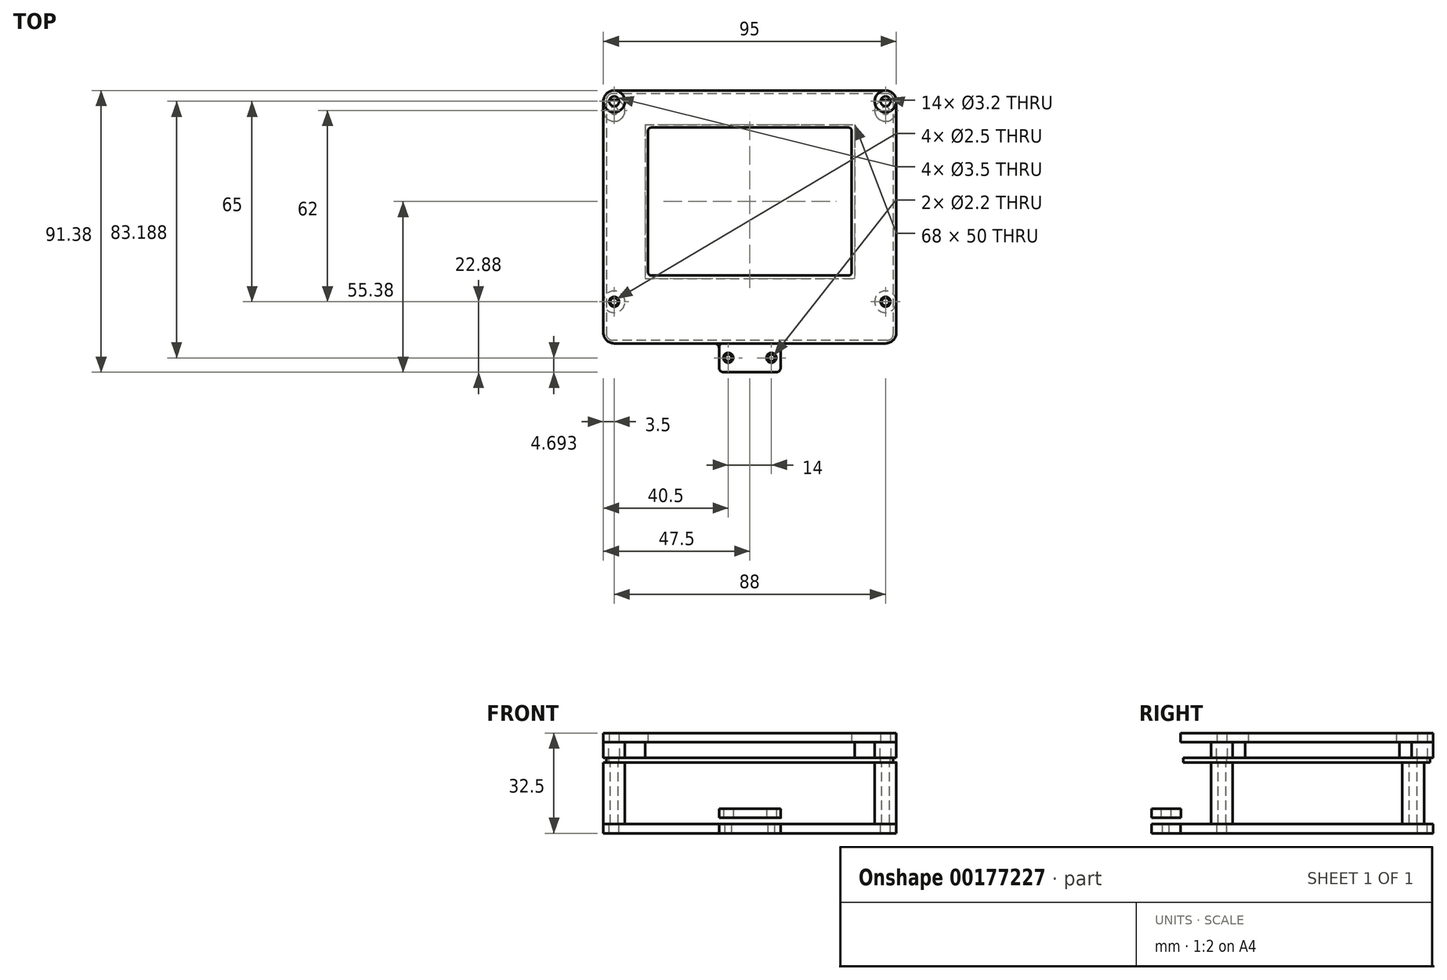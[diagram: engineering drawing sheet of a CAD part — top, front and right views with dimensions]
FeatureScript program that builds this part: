
annotation { "Feature Type Name" : "Feature", "Feature Type Description" : "" }
export const myFeature = defineFeature(function(context is Context, id is Id, definition is map)
    precondition{}
    {
        {
            var Q0;
            Q0=qCreatedBy(makeId("Top.planeOp"),FACE);
            var sketch = newSketch(context, id + "F0", { "sketchPlane" : qUnion([Q0])});
            skLineSegment(sketch, "E0.bottom", {"start": v(44, -41) * mm, "end": v(-44, -41) * mm});
            skLineSegment(sketch, "E0.top", {"start": v(44, 41) * mm, "end": v(-44, 41) * mm});
            skLineSegment(sketch, "E0.left", {"start": v(47.5, -37.5) * mm, "end": v(47.5, 37.5) * mm});
            skLineSegment(sketch, "E0.right", {"start": v(-47.5, -37.5) * mm, "end": v(-47.5, 37.5) * mm});
            skPoint(sketch, "E0.middle", {"position": v(0, 0) * mm});
            skLineSegment(sketch, "E1.top", {"start": v(44, 37.5) * mm, "end": v(-44, 37.5) * mm, "construction": true});
            skLineSegment(sketch, "E1.left", {"start": v(44, -27.5) * mm, "end": v(44, 37.5) * mm, "construction": true});
            skLineSegment(sketch, "E1.right", {"start": v(-44, -27.5) * mm, "end": v(-44, 37.5) * mm, "construction": true});
            skLineSegment(sketch, "E2", {"start": v(-44, -27.5) * mm, "end": v(44, -27.5) * mm, "construction": true});
            skPoint(sketch, "E1.bottom.end.orphan", {"position": v(-44, -37.5) * mm});
            skPoint(sketch, "E3.orphan", {"position": v(44, -37.5) * mm});
            skCircle(sketch, "E4", {"center": v(-44, 37.5) * mm, "radius": 1.6 * mm});
            skCircle(sketch, "E5", {"center": v(44, 37.5) * mm, "radius": 1.6 * mm});
            skCircle(sketch, "E6", {"center": v(44, -27.5) * mm, "radius": 1.6 * mm});
            skCircle(sketch, "E7", {"center": v(-44, -27.5) * mm, "radius": 1.6 * mm});
            skArc(sketch, "E8", {"start": v(-44, 41) * mm, "mid": v(-46.47, 39.97) * mm, "end": v(-47.5, 37.5) * mm});
            skArc(sketch, "E9", {"start": v(47.5, 37.5) * mm, "mid": v(46.47, 39.97) * mm, "end": v(44, 41) * mm});
            skPoint(sketch, "E10.visualSharp", {"position": v(47.5, -41) * mm});
            skArc(sketch, "E10.filletArc", {"start": v(44, -41) * mm, "mid": v(46.47, -39.97) * mm, "end": v(47.5, -37.5) * mm});
            skPoint(sketch, "E11.visualSharp", {"position": v(-47.5, -41) * mm});
            skArc(sketch, "E11.filletArc", {"start": v(-47.5, -37.5) * mm, "mid": v(-46.47, -39.97) * mm, "end": v(-44, -41) * mm});
            skPoint(sketch, "E12.orphan", {"position": v(-47.5, 41) * mm});
            skPoint(sketch, "E13.orphan", {"position": v(47.5, 41) * mm});
            skLineSegment(sketch, "E14.bottom", {"start": v(-32, 29) * mm, "end": v(32, 29) * mm});
            skLineSegment(sketch, "E14.top", {"start": v(-32, -19) * mm, "end": v(32, -19) * mm});
            skLineSegment(sketch, "E14.left", {"start": v(-33, 28) * mm, "end": v(-33, -18) * mm});
            skLineSegment(sketch, "E14.right", {"start": v(33, 28) * mm, "end": v(33, -18) * mm});
            skPoint(sketch, "E15.visualSharp", {"position": v(-33, 29) * mm});
            skArc(sketch, "E15.filletArc", {"start": v(-32, 29) * mm, "mid": v(-32.7, 28.7) * mm, "end": v(-33, 28) * mm});
            skPoint(sketch, "E16.visualSharp", {"position": v(33, 29) * mm});
            skArc(sketch, "E16.filletArc", {"start": v(33, 28) * mm, "mid": v(32.7, 28.7) * mm, "end": v(32, 29) * mm});
            skPoint(sketch, "E17.visualSharp", {"position": v(33, -19) * mm});
            skArc(sketch, "E17.filletArc", {"start": v(32, -19) * mm, "mid": v(32.7, -18.7) * mm, "end": v(33, -18) * mm});
            skPoint(sketch, "E18.visualSharp", {"position": v(-33, -19) * mm});
            skArc(sketch, "E18.filletArc", {"start": v(-33, -18) * mm, "mid": v(-32.7, -18.7) * mm, "end": v(-32, -19) * mm});
            skSolve(sketch);
        }
        {
            var Q0;
            Q0=makeQuery(id+"F0.imprint","IMPRINT",FACE,{"disambiguationData":[TD([[makeQuery(id+"F0.imprint","IMPRINT",EDGE,{"derivedFrom":sQuery(id+"F0.wireOp",EDGE,"E0.bottom")}),-1.0]])]});
            extrude(context, id + "F1", {"entities" : qUnion([Q0]), "depth" : 3 * mm});
        }
        {
            var Q0;
            Q0=makeQuery(id+"F1.opExtrude","CAP_FACE",FACE,{"disambiguationData":[OSD([sQuery(id+"F0.wireOp",EDGE,"E0.bottom"),sQuery(id+"F0.wireOp",EDGE,"E0.top"),sQuery(id+"F0.wireOp",EDGE,"E0.left"),sQuery(id+"F0.wireOp",EDGE,"E0.right"),sQuery(id+"F0.wireOp",EDGE,"E4"),sQuery(id+"F0.wireOp",EDGE,"E5"),sQuery(id+"F0.wireOp",EDGE,"E6"),sQuery(id+"F0.wireOp",EDGE,"E7"),sQuery(id+"F0.wireOp",EDGE,"E8"),sQuery(id+"F0.wireOp",EDGE,"E9"),sQuery(id+"F0.wireOp",EDGE,"E10.filletArc"),sQuery(id+"F0.wireOp",EDGE,"E11.filletArc"),sQuery(id+"F0.wireOp",EDGE,"E14.bottom"),sQuery(id+"F0.wireOp",EDGE,"E14.top"),sQuery(id+"F0.wireOp",EDGE,"E14.left"),sQuery(id+"F0.wireOp",EDGE,"E14.right"),sQuery(id+"F0.wireOp",EDGE,"E15.filletArc"),sQuery(id+"F0.wireOp",EDGE,"E16.filletArc"),sQuery(id+"F0.wireOp",EDGE,"E17.filletArc"),sQuery(id+"F0.wireOp",EDGE,"E18.filletArc")])],"isStart":true});
            var sketch = newSketch(context, id + "F2", { "sketchPlane" : qUnion([Q0])});
            skCircle(sketch, "E19", {"center": v(-44, 27.5) * mm, "radius": 1.75 * mm});
            skCircle(sketch, "E20", {"center": v(44, 27.5) * mm, "radius": 1.75 * mm});
            skCircle(sketch, "E21", {"center": v(44, -37.5) * mm, "radius": 1.75 * mm});
            skCircle(sketch, "E22", {"center": v(-44, -37.5) * mm, "radius": 1.75 * mm});
            skCircle(sketch, "E23", {"center": v(-44, -37.5) * mm, "radius": 3.5 * mm});
            skCircle(sketch, "E24", {"center": v(44, -37.5) * mm, "radius": 3.5 * mm});
            skCircle(sketch, "E25", {"center": v(44, 27.5) * mm, "radius": 3.5 * mm});
            skCircle(sketch, "E26", {"center": v(-44, 27.5) * mm, "radius": 3.5 * mm});
            skSolve(sketch);
        }
        {
            var Q0;
            Q0 = qSketchRegion(id + "F2", true);
            extrude(context, id + "F3", {"entities" : qUnion([Q0]), "depth" : 5 * mm});
        }
        {
            var Q0;
            Q0=makeQuery(id+"F3.opExtrude","CAP_FACE",FACE,{"disambiguationData":[OSD([sQuery(id+"F2.wireOp",EDGE,"E19"),sQuery(id+"F2.wireOp",EDGE,"E26")])],"isStart":false});
            var sketch = newSketch(context, id + "F4", { "sketchPlane" : qUnion([Q0])});
            skLineSegment(sketch, "E27.bottom", {"start": v(44.5, -40) * mm, "end": v(-44.5, -40) * mm});
            skLineSegment(sketch, "E27.top", {"start": v(44.5, 40) * mm, "end": v(-44.5, 40) * mm});
            skLineSegment(sketch, "E27.left", {"start": v(46.5, -38) * mm, "end": v(46.5, 38) * mm});
            skLineSegment(sketch, "E27.right", {"start": v(-46.5, -38) * mm, "end": v(-46.5, 38) * mm});
            skPoint(sketch, "E27.middle", {"position": v(0, 0) * mm});
            skPoint(sketch, "E28.visualSharp", {"position": v(-46.5, 40) * mm});
            skArc(sketch, "E28.filletArc", {"start": v(-44.5, 40) * mm, "mid": v(-45.91, 39.41) * mm, "end": v(-46.5, 38) * mm});
            skPoint(sketch, "E29.visualSharp", {"position": v(46.5, 40) * mm});
            skArc(sketch, "E29.filletArc", {"start": v(46.5, 38) * mm, "mid": v(45.91, 39.41) * mm, "end": v(44.5, 40) * mm});
            skPoint(sketch, "E30.visualSharp", {"position": v(46.5, -40) * mm});
            skArc(sketch, "E30.filletArc", {"start": v(44.5, -40) * mm, "mid": v(45.91, -39.41) * mm, "end": v(46.5, -38) * mm});
            skPoint(sketch, "E31.visualSharp", {"position": v(-46.5, -40) * mm});
            skArc(sketch, "E31.filletArc", {"start": v(-46.5, -38) * mm, "mid": v(-45.91, -39.41) * mm, "end": v(-44.5, -40) * mm});
            skCircle(sketch, "E32", {"center": v(-44, 27.5) * mm, "radius": 1.6 * mm});
            skCircle(sketch, "E33.0.1.0", {"center": v(-44, -37.5) * mm, "radius": 1.6 * mm});
            skCircle(sketch, "E33.1.0.0", {"center": v(44, 27.5) * mm, "radius": 1.6 * mm});
            skCircle(sketch, "E33.1.1.0", {"center": v(44, -37.5) * mm, "radius": 1.6 * mm});
            skCircle(sketch, "E33.2.0.0", {"center": v(132, 27.5) * mm, "radius": 1.6 * mm});
            skCircle(sketch, "E33.2.1.0", {"center": v(132, -37.5) * mm, "radius": 1.6 * mm});
            skLineSegment(sketch, "E33.direction1", {"start": v(-44, 27.5) * mm, "end": v(44, 27.5) * mm, "construction": true});
            skLineSegment(sketch, "E33.direction2", {"start": v(-44, 27.5) * mm, "end": v(-44, -37.5) * mm, "construction": true});
            skSolve(sketch);
        }
        {
            var Q0;
            Q0 = qSketchRegion(id + "F4", true);
            extrude(context, id + "F5", {"entities" : qUnion([Q0]), "depth" : 1.5 * mm});
        }
        {
            var Q0;
            Q0=makeQuery(id+"F5.opExtrude","CAP_FACE",FACE,{"disambiguationData":[OSD([sQuery(id+"F4.wireOp",EDGE,"E27.bottom"),sQuery(id+"F4.wireOp",EDGE,"E27.top"),sQuery(id+"F4.wireOp",EDGE,"E27.left"),sQuery(id+"F4.wireOp",EDGE,"E27.right"),sQuery(id+"F4.wireOp",EDGE,"E28.filletArc"),sQuery(id+"F4.wireOp",EDGE,"E29.filletArc"),sQuery(id+"F4.wireOp",EDGE,"E30.filletArc"),sQuery(id+"F4.wireOp",EDGE,"E31.filletArc"),sQuery(id+"F4.wireOp",EDGE,"E32"),sQuery(id+"F4.wireOp",EDGE,"E33.0.1.0"),sQuery(id+"F4.wireOp",EDGE,"E33.1.0.0"),sQuery(id+"F4.wireOp",EDGE,"E33.1.1.0")])],"isStart":false});
            var sketch = newSketch(context, id + "F6", { "sketchPlane" : qUnion([Q0])});
            skCircle(sketch, "E34", {"center": v(-44, 27.5) * mm, "radius": 1.25 * mm});
            skCircle(sketch, "E35", {"center": v(-44, 27.5) * mm, "radius": 3.5 * mm});
            skCircle(sketch, "E36.0.1.0", {"center": v(-44, -34.5) * mm, "radius": 1.25 * mm});
            skCircle(sketch, "E36.0.1.1", {"center": v(-44, -34.5) * mm, "radius": 3.5 * mm});
            skCircle(sketch, "E36.1.0.0", {"center": v(44, 27.5) * mm, "radius": 1.25 * mm});
            skCircle(sketch, "E36.1.0.1", {"center": v(44, 27.5) * mm, "radius": 3.5 * mm});
            skCircle(sketch, "E36.1.1.0", {"center": v(44, -34.5) * mm, "radius": 1.25 * mm});
            skCircle(sketch, "E36.1.1.1", {"center": v(44, -34.5) * mm, "radius": 3.5 * mm});
            skLineSegment(sketch, "E36.direction1", {"start": v(-44, 27.5) * mm, "end": v(44, 27.5) * mm, "construction": true});
            skLineSegment(sketch, "E36.direction2", {"start": v(-44, 27.5) * mm, "end": v(-44, -34.5) * mm, "construction": true});
            skSolve(sketch);
        }
        {
            var Q0;
            Q0 = qSketchRegion(id + "F6", true);
            extrude(context, id + "F7", {"entities" : qUnion([Q0]), "depth" : 20 * mm});
        }
        {
            var Q0;
            Q0=makeQuery(id+"F7.opExtrude","CAP_FACE",FACE,{"disambiguationData":[OSD([sQuery(id+"F6.wireOp",EDGE,"E34"),sQuery(id+"F6.wireOp",EDGE,"E35")])],"isStart":false});
            var sketch = newSketch(context, id + "F8", { "sketchPlane" : qUnion([Q0])});
            skLineSegment(sketch, "E37.bottom", {"start": v(44, -41) * mm, "end": v(-44, -41) * mm});
            skLineSegment(sketch, "E37.top", {"start": v(44, 41) * mm, "end": v(11.5, 41) * mm});
            skLineSegment(sketch, "E37.left", {"start": v(47.5, -37.5) * mm, "end": v(47.5, 37.5) * mm});
            skLineSegment(sketch, "E37.right", {"start": v(-47.5, -37.5) * mm, "end": v(-47.5, 37.5) * mm});
            skPoint(sketch, "E37.middle", {"position": v(0, 0) * mm});
            skPoint(sketch, "E38.visualSharp", {"position": v(47.5, 41) * mm});
            skArc(sketch, "E38.filletArc", {"start": v(47.5, 37.5) * mm, "mid": v(46.47, 39.97) * mm, "end": v(44, 41) * mm});
            skPoint(sketch, "E39.visualSharp", {"position": v(47.5, -41) * mm});
            skArc(sketch, "E39.filletArc", {"start": v(44, -41) * mm, "mid": v(46.47, -39.97) * mm, "end": v(47.5, -37.5) * mm});
            skPoint(sketch, "E40.visualSharp", {"position": v(-47.5, -41) * mm});
            skArc(sketch, "E40.filletArc", {"start": v(-47.5, -37.5) * mm, "mid": v(-46.47, -39.97) * mm, "end": v(-44, -41) * mm});
            skPoint(sketch, "E41.visualSharp", {"position": v(-47.5, 41) * mm});
            skArc(sketch, "E41.filletArc", {"start": v(-44, 41) * mm, "mid": v(-46.47, 39.97) * mm, "end": v(-47.5, 37.5) * mm});
            skCircle(sketch, "E42", {"center": v(-44, 27.5) * mm, "radius": 1.6 * mm});
            skCircle(sketch, "E43.0.1.0", {"center": v(-44, -37.5) * mm, "radius": 1.6 * mm});
            skCircle(sketch, "E43.1.0.0", {"center": v(44, 27.5) * mm, "radius": 1.6 * mm});
            skCircle(sketch, "E43.1.1.0", {"center": v(44, -37.5) * mm, "radius": 1.6 * mm});
            skLineSegment(sketch, "E43.direction1", {"start": v(-44, 27.5) * mm, "end": v(44, 27.5) * mm, "construction": true});
            skLineSegment(sketch, "E43.direction2", {"start": v(-44, 27.5) * mm, "end": v(-44, -37.5) * mm, "construction": true});
            skLineSegment(sketch, "E44.top", {"start": v(8.5, 50.37) * mm, "end": v(-8.5, 50.37) * mm});
            skLineSegment(sketch, "E44.left", {"start": v(10, 42.5) * mm, "end": v(10, 48.87) * mm});
            skLineSegment(sketch, "E44.right", {"start": v(-10, 42.5) * mm, "end": v(-10, 48.87) * mm});
            skPoint(sketch, "E44.middle", {"position": v(0, 41) * mm});
            skPoint(sketch, "E44.bottom.end.orphan", {"position": v(-10, 31.62) * mm});
            skPoint(sketch, "E45.orphan", {"position": v(10, 31.62) * mm});
            skLineSegment(sketch, "E46.trimOffspring", {"start": v(-11.5, 41) * mm, "end": v(-44, 41) * mm});
            skPoint(sketch, "E47.visualSharp", {"position": v(-10, 41) * mm});
            skArc(sketch, "E47.filletArc", {"start": v(-11.5, 41) * mm, "mid": v(-10.44, 41.44) * mm, "end": v(-10, 42.5) * mm});
            skPoint(sketch, "E48.visualSharp", {"position": v(10, 41) * mm});
            skArc(sketch, "E48.filletArc", {"start": v(10, 42.5) * mm, "mid": v(10.44, 41.44) * mm, "end": v(11.5, 41) * mm});
            skPoint(sketch, "E49.visualSharp", {"position": v(10, 50.37) * mm});
            skArc(sketch, "E49.filletArc", {"start": v(10, 48.87) * mm, "mid": v(9.56, 49.94) * mm, "end": v(8.5, 50.37) * mm});
            skPoint(sketch, "E50.visualSharp", {"position": v(-10, 50.37) * mm});
            skArc(sketch, "E50.filletArc", {"start": v(-8.5, 50.37) * mm, "mid": v(-9.56, 49.94) * mm, "end": v(-10, 48.87) * mm});
            skLineSegment(sketch, "E51", {"start": v(-10, 45.69) * mm, "end": v(10, 45.69) * mm, "construction": true});
            skCircle(sketch, "E52", {"center": v(-7, 45.69) * mm, "radius": 1.1 * mm});
            skCircle(sketch, "E53", {"center": v(7, 45.69) * mm, "radius": 1.1 * mm});
            skSolve(sketch);
        }
        {
            var Q0;
            Q0 = qSketchRegion(id + "F8", true);
            extrude(context, id + "F9", {"entities" : qUnion([Q0]), "depth" : 3 * mm});
        }
        {
            var Q0;
            Q0=makeQuery(id+"F9.opExtrude","CAP_FACE",FACE,{"disambiguationData":[OSD([sQuery(id+"F8.wireOp",EDGE,"E37.bottom"),sQuery(id+"F8.wireOp",EDGE,"E37.top"),sQuery(id+"F8.wireOp",EDGE,"E37.left"),sQuery(id+"F8.wireOp",EDGE,"E37.right"),sQuery(id+"F8.wireOp",EDGE,"E38.filletArc"),sQuery(id+"F8.wireOp",EDGE,"E39.filletArc"),sQuery(id+"F8.wireOp",EDGE,"E40.filletArc"),sQuery(id+"F8.wireOp",EDGE,"E41.filletArc"),sQuery(id+"F8.wireOp",EDGE,"E42"),sQuery(id+"F8.wireOp",EDGE,"E43.0.1.0"),sQuery(id+"F8.wireOp",EDGE,"E43.1.0.0"),sQuery(id+"F8.wireOp",EDGE,"E43.1.1.0"),sQuery(id+"F8.wireOp",EDGE,"E44.top"),sQuery(id+"F8.wireOp",EDGE,"E44.left"),sQuery(id+"F8.wireOp",EDGE,"E44.right"),sQuery(id+"F8.wireOp",EDGE,"E46.trimOffspring"),sQuery(id+"F8.wireOp",EDGE,"E47.filletArc"),sQuery(id+"F8.wireOp",EDGE,"E48.filletArc"),sQuery(id+"F8.wireOp",EDGE,"E49.filletArc"),sQuery(id+"F8.wireOp",EDGE,"E50.filletArc"),sQuery(id+"F8.wireOp",EDGE,"E52"),sQuery(id+"F8.wireOp",EDGE,"E53")])],"isStart":true});
            cPlane(context, id + "F10", {"entities" : qUnion([Q0]), "cplaneType" : CPlaneType.OFFSET, "offset" : 2 * mm, "width" : 150 * mm, "height" : 150 * mm});
        }
        {
            var Q0;
            Q0=qCreatedBy(id+"F10.planeOp",FACE);
            var sketch = newSketch(context, id + "F11", { "sketchPlane" : qUnion([Q0])});
            skLineSegment(sketch, "E54.0", {"start": v(10, -42.37) * mm, "end": v(10, -48.87) * mm});
            skLineSegment(sketch, "E55.0", {"start": v(8.5, -50.37) * mm, "end": v(-8.5, -50.37) * mm});
            skLineSegment(sketch, "E56.0", {"start": v(-10, -42.37) * mm, "end": v(-10, -48.87) * mm});
            skLineSegment(sketch, "E57", {"start": v(-8.5, -40.87) * mm, "end": v(8.5, -40.87) * mm});
            skPoint(sketch, "E58.newPointA", {"position": v(10, -48.87) * mm});
            skPoint(sketch, "E58.newPointB", {"position": v(8.5, -50.37) * mm});
            skArc(sketch, "E58.filletArc", {"start": v(8.5, -50.37) * mm, "mid": v(9.56, -49.94) * mm, "end": v(10, -48.87) * mm});
            skPoint(sketch, "E59.newPointA", {"position": v(-8.5, -50.37) * mm});
            skPoint(sketch, "E59.newPointB", {"position": v(-10, -48.87) * mm});
            skArc(sketch, "E59.filletArc", {"start": v(-10, -48.87) * mm, "mid": v(-9.56, -49.94) * mm, "end": v(-8.5, -50.37) * mm});
            skPoint(sketch, "E60.newPointA", {"position": v(-10, -42.5) * mm});
            skArc(sketch, "E60.filletArc", {"start": v(-8.5, -40.87) * mm, "mid": v(-9.56, -41.31) * mm, "end": v(-10, -42.37) * mm});
            skPoint(sketch, "E61.newPointB", {"position": v(10, -42.5) * mm});
            skArc(sketch, "E61.filletArc", {"start": v(10, -42.37) * mm, "mid": v(9.56, -41.31) * mm, "end": v(8.5, -40.88) * mm});
            skCircle(sketch, "E62", {"center": v(-7, -45.69) * mm, "radius": 1.6 * mm});
            skCircle(sketch, "E63", {"center": v(7, -45.69) * mm, "radius": 1.6 * mm});
            skSolve(sketch);
        }
        {
            var Q0;
            Q0 = qSketchRegion(id + "F11", true);
            extrude(context, id + "F12", {"entities" : qUnion([Q0]), "depth" : 3 * mm});
        }
        {
            var Q0;
            Q0=makeQuery(id+"F5.opExtrude","CAP_FACE",FACE,{"disambiguationData":[OSD([sQuery(id+"F4.wireOp",EDGE,"E27.bottom"),sQuery(id+"F4.wireOp",EDGE,"E27.top"),sQuery(id+"F4.wireOp",EDGE,"E27.left"),sQuery(id+"F4.wireOp",EDGE,"E27.right"),sQuery(id+"F4.wireOp",EDGE,"E28.filletArc"),sQuery(id+"F4.wireOp",EDGE,"E29.filletArc"),sQuery(id+"F4.wireOp",EDGE,"E30.filletArc"),sQuery(id+"F4.wireOp",EDGE,"E31.filletArc"),sQuery(id+"F4.wireOp",EDGE,"E32"),sQuery(id+"F4.wireOp",EDGE,"E33.0.1.0"),sQuery(id+"F4.wireOp",EDGE,"E33.1.0.0"),sQuery(id+"F4.wireOp",EDGE,"E33.1.1.0")])],"isStart":true});
            var sketch = newSketch(context, id + "F13", { "sketchPlane" : qUnion([Q0])});
            skLineSegment(sketch, "E64.bottom", {"start": v(-34, 30) * mm, "end": v(34, 30) * mm});
            skLineSegment(sketch, "E64.top", {"start": v(-34, -20) * mm, "end": v(34, -20) * mm});
            skLineSegment(sketch, "E64.left", {"start": v(-34, 30) * mm, "end": v(-34, -20) * mm});
            skLineSegment(sketch, "E64.right", {"start": v(34, 30) * mm, "end": v(34, -20) * mm});
            skSolve(sketch);
        }
        {
            var Q0;
            Q0 = qSketchRegion(id + "F13", true);
            var Q1;
            Q1=makeQuery(id+"F1.opExtrude","CAP_FACE",FACE,{"disambiguationData":[OSD([sQuery(id+"F0.wireOp",EDGE,"E0.bottom"),sQuery(id+"F0.wireOp",EDGE,"E0.top"),sQuery(id+"F0.wireOp",EDGE,"E0.left"),sQuery(id+"F0.wireOp",EDGE,"E0.right"),sQuery(id+"F0.wireOp",EDGE,"E4"),sQuery(id+"F0.wireOp",EDGE,"E5"),sQuery(id+"F0.wireOp",EDGE,"E6"),sQuery(id+"F0.wireOp",EDGE,"E7"),sQuery(id+"F0.wireOp",EDGE,"E8"),sQuery(id+"F0.wireOp",EDGE,"E9"),sQuery(id+"F0.wireOp",EDGE,"E10.filletArc"),sQuery(id+"F0.wireOp",EDGE,"E11.filletArc"),sQuery(id+"F0.wireOp",EDGE,"E14.bottom"),sQuery(id+"F0.wireOp",EDGE,"E14.top"),sQuery(id+"F0.wireOp",EDGE,"E14.left"),sQuery(id+"F0.wireOp",EDGE,"E14.right"),sQuery(id+"F0.wireOp",EDGE,"E15.filletArc"),sQuery(id+"F0.wireOp",EDGE,"E16.filletArc"),sQuery(id+"F0.wireOp",EDGE,"E17.filletArc"),sQuery(id+"F0.wireOp",EDGE,"E18.filletArc")])],"isStart":true});
            extrude(context, id + "F14", {"entities" : qUnion([Q0]), "operationType" : NewBodyOperationType.ADD, "endBound" : BoundingType.UP_TO_SURFACE, "endBoundEntityFace" : qUnion([Q1]), "depth" : 25 * mm});
        }
        {
            var Q0;
            Q0=makeQuery(id+"F5.opExtrude","SWEPT_BODY",BODY,{"disambiguationData":[OSD([sQuery(id+"F4.wireOp",EDGE,"E33.2.0.0")])]});
            deleteBodies(context, id + "F15", {"entities" : qUnion([Q0])});
        }
        {
            var Q0;
            Q0=makeQuery(id+"F5.opExtrude","SWEPT_BODY",BODY,{"disambiguationData":[OSD([sQuery(id+"F4.wireOp",EDGE,"E33.2.1.0")])]});
            deleteBodies(context, id + "F16", {"entities" : qUnion([Q0])});
        }
    });
